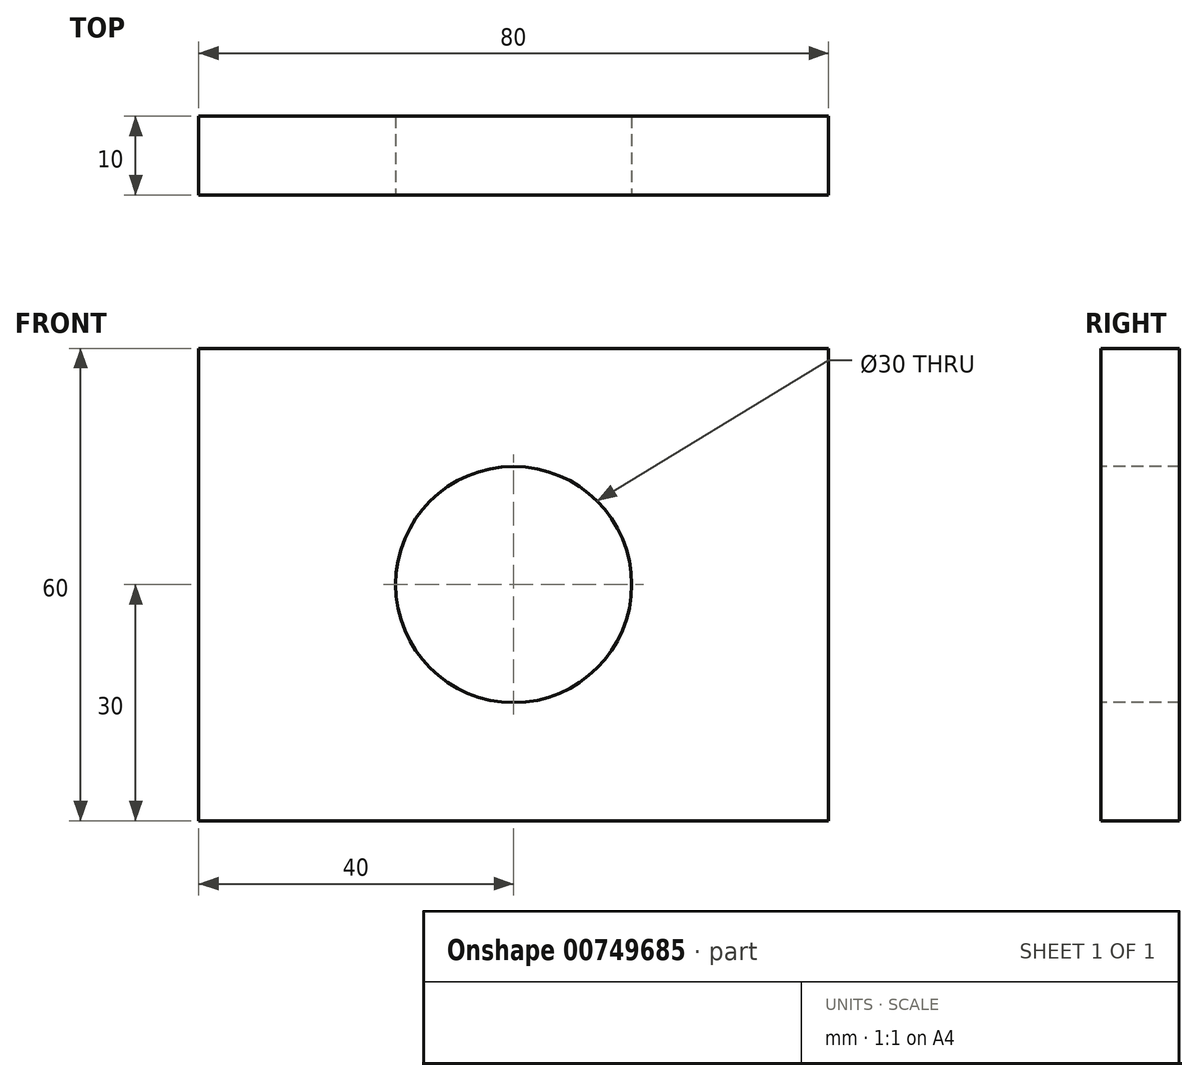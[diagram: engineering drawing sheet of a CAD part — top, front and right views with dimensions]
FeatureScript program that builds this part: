
annotation { "Feature Type Name" : "Feature", "Feature Type Description" : "" }
export const myFeature = defineFeature(function(context is Context, id is Id, definition is map)
    precondition{}
    {
        {
            var Q0;
            Q0=qCreatedBy(makeId("Front.planeOp"),FACE);
            var sketch = newSketch(context, id + "F0", { "sketchPlane" : qUnion([Q0])});
            skLineSegment(sketch, "E0.bottom", {"start": v(0, 0) * mm, "end": v(80, 0) * mm});
            skLineSegment(sketch, "E0.top", {"start": v(0, 60) * mm, "end": v(80, 60) * mm});
            skLineSegment(sketch, "E0.left", {"start": v(0, 0) * mm, "end": v(0, 60) * mm});
            skLineSegment(sketch, "E0.right", {"start": v(80, 0) * mm, "end": v(80, 60) * mm});
            skSolve(sketch);
        }
        {
            var Q0;
            Q0 = qSketchRegion(id + "F0", true);
            extrude(context, id + "F1", {"entities" : qUnion([Q0]), "depth" : 10 * mm, "offsetDistance" : 25 * mm});
        }
        {
            var Q0;
            Q0=makeQuery(id+"F1.opExtrude","CAP_FACE",FACE,{"disambiguationData":[OSD([sQuery(id+"F0.wireOp",EDGE,"E0.bottom"),sQuery(id+"F0.wireOp",EDGE,"E0.top"),sQuery(id+"F0.wireOp",EDGE,"E0.left"),sQuery(id+"F0.wireOp",EDGE,"E0.right")])],"isStart":false});
            var sketch = newSketch(context, id + "F2", { "sketchPlane" : qUnion([Q0])});
            skCircle(sketch, "E1", {"center": v(40, 30) * mm, "radius": 15 * mm});
            skPoint(sketch, "E1.centerSnap0", {"position": v(80, 30) * mm});
            skPoint(sketch, "E1.centerSnap1", {"position": v(40, 60) * mm});
            skSolve(sketch);
        }
        {
            var Q0;
            Q0=makeQuery(id+"F2.imprint","IMPRINT",FACE,{"disambiguationData":[TD([[makeQuery(id+"F2.imprint","IMPRINT",EDGE,{"derivedFrom":sQuery(id+"F2.wireOp",EDGE,"E1")}),1.0]])]});
            extrude(context, id + "F3", {"entities" : qUnion([Q0]), "operationType" : NewBodyOperationType.REMOVE, "endBound" : BoundingType.THROUGH_ALL, "oppositeDirection" : true, "depth" : 25 * mm, "offsetDistance" : 25 * mm});
        }
    });
